# Revit family: ESHL-L-280-xxx-840-SMx
name_source: partatom
category: Oprawy oświetleniowe
revit_build: Autodesk Revit 2017 (Build: 20190507_1515(x64)
units: mm (PartAtom-declared; Revit-internal decimal feet)

## family parameters
Numer OmniClass = 23.80.70.11
Obiekt nadrzędny = Powierzchnia
Punkt obliczania pomieszczeń = Nie
Tnij formami wycięć po wczytaniu = Nie
Typ części = Normalny
Tytuł OmniClass = Luminaries for Internal Lighting
Współdzielony = Nie
Wymiar okrągłego złącza = Użyj średnicy
Źródło światła = Tak

## types (4) — shared parameters
Emituj kształt widoczny w renderingu = Nie
Emituj z długości prostokąta = 256 mm  [stored 0.839895 ft]
Emituj z szerokości prostokąta = 1496 mm  [stored 4.90814 ft]
Filtr koloru = 16777215
Kod zespołu = D5020200
Lampa = LED
Odchylenie kierunku = 90.00°
Producent = RIDI Leuchten GmbH
URL = www.ridi.de
Zmiana temperatury barwowej przyciemniania lampy = <Brak>
brand = RIDI
conformity mark = CE
electrical safety class = 1
height = 85 mm  [stored 0.278871 ft]
ingress protection (IP) code = IP40
length = 1548 mm  [stored 5.07874 ft]
nominal frequency = 50-60Hz
nominal voltage = 230
voltage type (AC, DC, UC) = AC
weight = 15.00 kg
width = 312 mm  [stored 1.02362 ft]
zero-valued in all types: Domyślna rzędna

## per-type parameters (varying)
| type | Model | Obciążenie pozorne | Plik sieci fotometrycznej | rated input power |
| ESHL-L 280/1240-840 SM | 0850595 | 96 VA | ESHL-L 2801240-840 SM.IES | 96 |
| ESHL-L 280/1240-840 SM-DA | 0860595 | 96 VA | ESHL-L 2801240-840 SM.IES | 96 |
| ESHL-L 280/1870-840 SM | 0850627 | 140 VA | ESHL-L 2801870-840 SM.IES | 140 |
| ESHL-L 280/1870-840 SM-DA | 0860627 | 140 VA | ESHL-L 2801870-840 SM.IES | 140 |

note: column(s) folded — value = type name in every type: product name

note: [stored X ft] marks values corroborated as IEEE doubles in the binary element streams (Revit-internal decimal feet)
